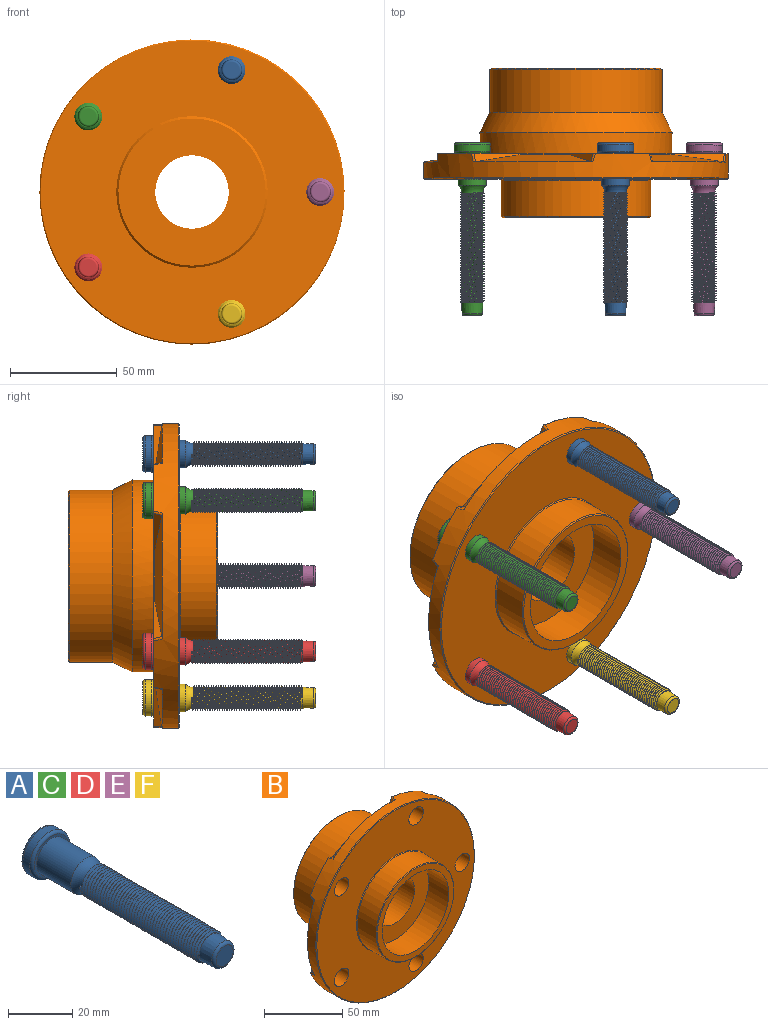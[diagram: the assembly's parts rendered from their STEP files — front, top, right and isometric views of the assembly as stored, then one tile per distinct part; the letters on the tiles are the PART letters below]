
ASSEMBLY  parts=6 mates=4
PART A: 15 faces, bbox 21.6x81x21.6 mm
  f0: cylinder r=6.5mm len=15mm, axis (0,1,0), area 612.6mm2, adj f3,f7
  f1: cylinder r=8.53mm len=17.05mm, axis (0,-1,0), area 160.7mm2, adj f5,f6
  f2: plane 15.05x15.05mm, normal (0,1,0), area 178mm2, adj f6
  f3: plane 15.05x15.05mm, normal (0,-1,0), area 45.2mm2, adj f0,f5
  f4: cylinder r=5mm len=51.43mm, axis (0,1,0), area 484.4mm2, adj f7,f9,f10,f11,f12
  f5: torus R=7.53mm, axis (0,1,0), area 80.6mm2, adj f1,f3
  f6: torus R=7.53mm, axis (0,1,0), area 80.6mm2, adj f1,f2
  f7: torus R=10mm, axis (0,1,0), area 127.8mm2, adj f0,f4,f8,f9
  f8: plane 0.83x0.75mm, normal (0,0,1), area 0.3mm2, adj f7,f9,f11
  f9: bspline ~51.86x11.49mm, area 1315.1mm2, adj f4,f7,f8,f10,f11
  f10: plane 0.87x0.75mm, normal (0,0,-1), area 0.3mm2, adj f4,f9,f11
  f11: bspline ~51.86x13.28mm, area 1316.1mm2, adj f4,f8,f9,f10
  f12: cone r=5mm half-angle=3deg, axis (0,1,0), area 154.7mm2, adj f4,f14
  f13: plane 7.47x7.47mm, normal (0,-1,0), area 43.9mm2, adj f14
  f14: torus R=3.74mm, axis (0,-1,0), area 41.6mm2, adj f12,f13
PART B: 61 faces, bbox 143.1x70.1x143.1 mm
  f0: cylinder r=6.5mm len=13mm, axis (0,1,0), area 490.1mm2, adj f13,f20
  f1: cylinder r=6.5mm len=13mm, axis (0,1,0), area 490.1mm2, adj f13,f20
  f2: cylinder r=6.5mm len=13mm, axis (0,1,0), area 490.1mm2, adj f13,f20
  f3: cylinder r=6.5mm len=13mm, axis (0,1,0), area 490.1mm2, adj f13,f20
  f4: cylinder r=48.47mm len=17.55mm, axis (0,-1,0), area 10.9mm2, adj f13,f25,f38,f54
  f5: cone r=71.5mm half-angle=81.4deg, axis (0,-1,0), area 959.8mm2, adj f6,f14,f32,f34,f36,f39,f40,f41
  f6: cylinder r=48.47mm len=20.63mm, axis (0,-1,0), area 10.9mm2, adj f5,f13,f39,f41
  f7: cone r=71.5mm half-angle=81.4deg, axis (0,-1,0), area 959.8mm2, adj f8,f14,f30,f33,f42,f43,f44,f45
  f8: cylinder r=48.47mm len=21.69mm, axis (0,-1,0), area 10.9mm2, adj f7,f13,f42,f45
  f9: cone r=71.5mm half-angle=81.4deg, axis (0,-1,0), area 959.8mm2, adj f10,f14,f29,f31,f46,f47,f49,f50
  f10: cylinder r=48.47mm len=20.63mm, axis (0,-1,0), area 10.9mm2, adj f9,f13,f46,f50
  f11: cone r=71.5mm half-angle=81.4deg, axis (0,-1,0), area 959.8mm2, adj f12,f14,f26,f28,f48,f51,f52,f53
  f12: cylinder r=48.47mm len=17.55mm, axis (0,-1,0), area 10.9mm2, adj f11,f13,f51,f53
  f13: plane 141.98x136.37mm, normal (0,1,0), area 4137.9mm2, adj f0,f1,f2,f3,f4,f6,f8,f10
  f14: cylinder r=71.5mm len=143mm, axis (0,1,0), area 3927.1mm2, adj f5,f7,f9,f11,f13,f25,f36,f37
  f15: cylinder r=45mm len=90mm, axis (0,-1,0), area 2827.4mm2, adj f13,f24
  f16: plane 79.72x79.72mm, normal (0,1,0), area 4062mm2, adj f21,f57
  f17: cylinder r=30mm len=60mm, axis (0,1,0), area 3392.9mm2, adj f19,f22
  f18: cylinder r=35mm len=70mm, axis (0,1,0), area 3738.5mm2, adj f58,f59
  f19: plane 69x69mm, normal (0,-1,0), area 911.8mm2, adj f17,f59
  f20: plane 142x142mm, normal (0,-1,0), area 11213.9mm2, adj f0,f1,f2,f3,f56,f58,f60
  f21: cylinder r=17.2mm len=52mm, axis (0,1,0), area 5619.7mm2, adj f16,f22
  f22: plane 60x60mm, normal (0,-1,0), area 1898mm2, adj f17,f21
  f23: cylinder r=40.36mm len=80.72mm, axis (0,1,0), area 5127.6mm2, adj f24,f57
  f24: cone r=45mm half-angle=26.6deg, axis (0,-1,0), area 2782.3mm2, adj f15,f23
  f25: cone r=71.5mm half-angle=81.4deg, axis (0,-1,0), area 959.8mm2, adj f4,f14,f27,f35,f37,f38,f54,f55
  f26: plane 24.12x4.41mm, normal (0.17,0.26,0.95), area 56.1mm2, adj f11,f13,f52,f53
  f27: plane 24.12x4.41mm, normal (0.17,0.26,-0.95), area 56.1mm2, adj f13,f25,f54,f55
  f28: plane 24.3x4.38mm, normal (0.96,0.26,-0.13), area 56.1mm2, adj f11,f13,f48,f51
  f29: plane 21.71x11.65mm, normal (-0.85,0.26,0.45), area 56.1mm2, adj f9,f13,f49,f50
  f30: plane 17.74x17.43mm, normal (-0.69,0.26,-0.67), area 56.1mm2, adj f7,f13,f44,f45
  f31: plane 22.1x11.47mm, normal (0.42,0.26,0.87), area 56.1mm2, adj f9,f13,f46,f47
  f32: plane 22.1x11.47mm, normal (0.42,0.26,-0.87), area 56.1mm2, adj f5,f13,f40,f41
  f33: plane 17.74x17.43mm, normal (-0.69,0.26,0.67), area 56.1mm2, adj f7,f13,f42,f43
  f34: plane 21.71x11.65mm, normal (-0.85,0.26,-0.45), area 56.1mm2, adj f5,f13,f36,f39
  f35: plane 24.3x4.38mm, normal (0.96,0.26,0.13), area 56.1mm2, adj f13,f25,f37,f38
  f36: bspline ~4.42x2.17mm, area 5mm2, adj f5,f13,f14,f34
  f37: bspline ~4.42x1.6mm, area 5mm2, adj f13,f14,f25,f35
  f38: bspline ~1.05x1.02mm, area 0.5mm2, adj f4,f13,f25,f35
  f39: bspline ~1.02x1mm, area 0.5mm2, adj f5,f6,f13,f34
  f40: bspline ~4.42x1.99mm, area 5mm2, adj f5,f13,f14,f32
  f41: bspline ~1.14x1.02mm, area 0.5mm2, adj f5,f6,f13,f32
  f42: bspline ~1.13x1.02mm, area 0.5mm2, adj f7,f8,f13,f33
  f43: bspline ~4.42x2.18mm, area 5mm2, adj f7,f13,f14,f33
  f44: bspline ~4.42x2.18mm, area 5mm2, adj f7,f13,f14,f30
  f45: bspline ~1.13x1.02mm, area 0.5mm2, adj f7,f8,f13,f30
  f46: bspline ~1.14x1.02mm, area 0.5mm2, adj f9,f10,f13,f31
  f47: bspline ~4.42x1.99mm, area 5mm2, adj f9,f13,f14,f31
  f48: bspline ~4.42x1.6mm, area 5mm2, adj f11,f13,f14,f28
  f49: bspline ~4.42x2.17mm, area 5mm2, adj f9,f13,f14,f29
  f50: bspline ~1.02x1mm, area 0.5mm2, adj f9,f10,f13,f29
  f51: bspline ~1.05x1.02mm, area 0.5mm2, adj f11,f12,f13,f28
  f52: bspline ~4.42x1.94mm, area 5mm2, adj f11,f13,f14,f26
  f53: bspline ~1.02x0.85mm, area 0.5mm2, adj f11,f12,f13,f26
  f54: bspline ~1.02x0.85mm, area 0.5mm2, adj f4,f13,f25,f27
  f55: bspline ~4.42x1.94mm, area 5mm2, adj f13,f14,f25,f27
  f56: cylinder r=6.5mm len=13mm, axis (0,1,0), area 490.1mm2, adj f13,f20
  f57: cone r=39.86mm half-angle=45deg, axis (0,-1,0), area 178.2mm2, adj f16,f23
  f58: cone r=35mm half-angle=45deg, axis (0,1,0), area 156.6mm2, adj f18,f20
  f59: cone r=34.5mm half-angle=45deg, axis (0,1,0), area 154.4mm2, adj f18,f19
  f60: cone r=71mm half-angle=45deg, axis (0,1,0), area 316.6mm2, adj f14,f20
PART C: same geometry as A
PART D: same geometry as A
PART E: same geometry as A
PART F: same geometry as A
PLACE A at identity
PLACE B at identity fixed
PLACE C t=(-67.18,0,-21.83)mm
PLACE D t=(-67.18,0,-92.47)mm
PLACE E t=(41.52,0,-57.15)mm
PLACE F t=(0,0,-114.3)mm
MATE fastened F.f0 <-> B.f2  axis (0,-1,0) through (18.57,0,-57.15)mm
MATE fastened E.f0 <-> B.f3  axis (0,-1,0) through (60.09,0,0)mm
MATE fastened D.f0 <-> B.f1  axis (0,-1,0) through (-48.61,0,-35.32)mm
MATE fastened C.f0 <-> B.f0  axis (0,-1,0) through (-48.61,0,35.32)mm
